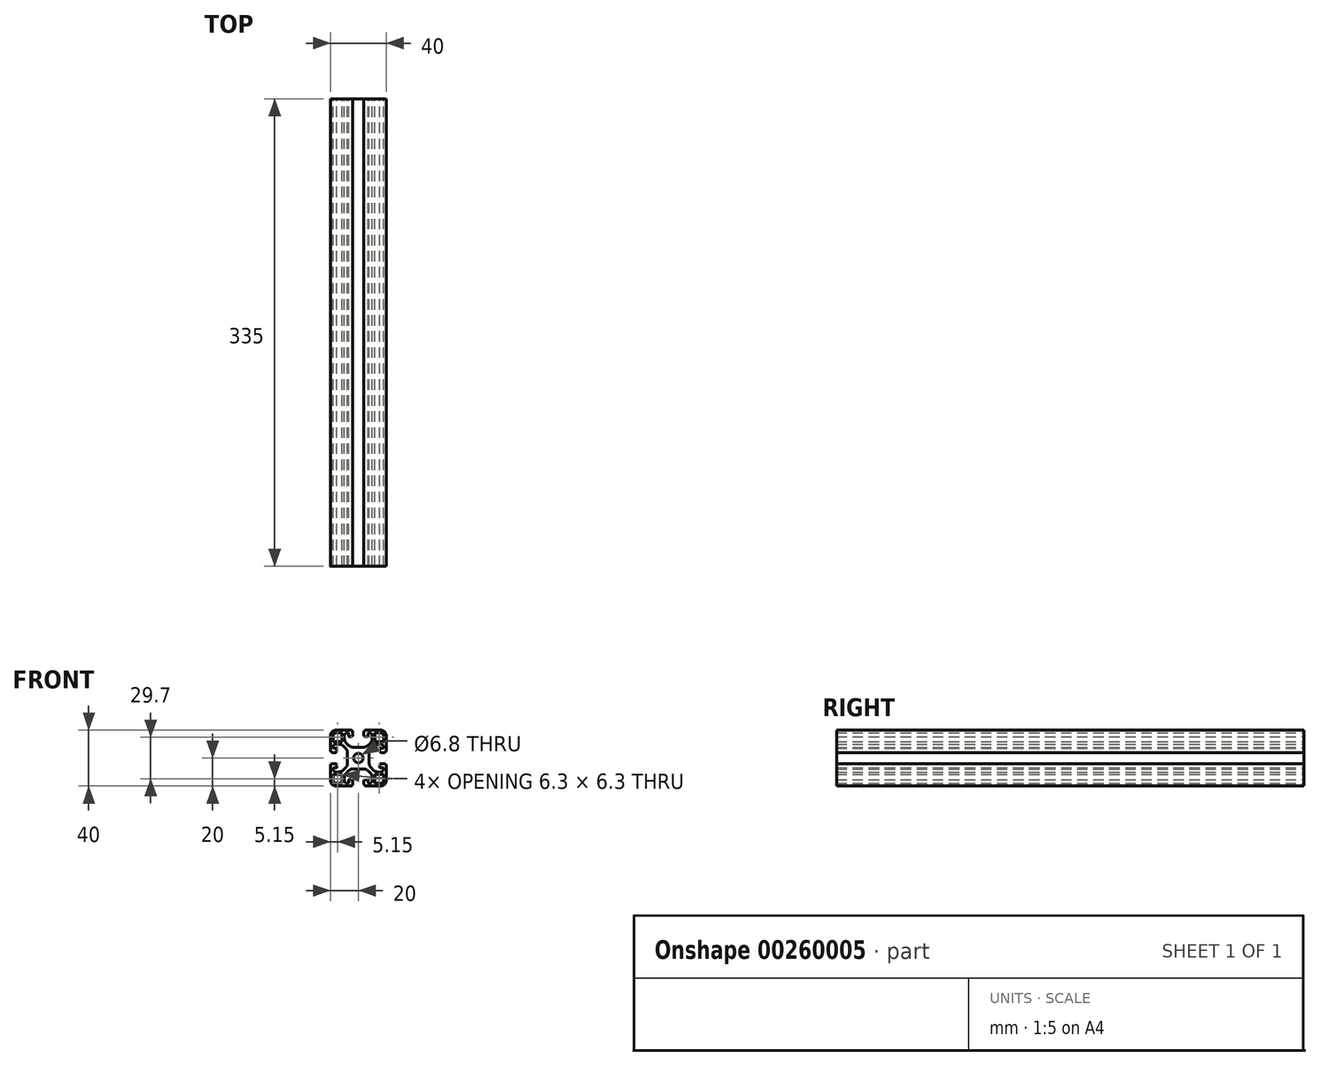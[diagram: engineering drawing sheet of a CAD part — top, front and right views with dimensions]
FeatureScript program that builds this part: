
annotation { "Feature Type Name" : "Feature", "Feature Type Description" : "" }
export const myFeature = defineFeature(function(context is Context, id is Id, definition is map)
    precondition{}
    {
        {
            var Q0;
            Q0=qCreatedBy(makeId("Front.planeOp"),FACE);
            var sketch = newSketch(context, id + "F0", { "sketchPlane" : qUnion([Q0])});
            skCircle(sketch, "E0", {"center": v(0, 0) * mm, "radius": 3.4 * mm});
            skLineSegment(sketch, "E1", {"start": v(0, 0) * mm, "end": v(20, 0) * mm, "construction": true});
            skLineSegment(sketch, "E2", {"start": v(0, 0) * mm, "end": v(20, 20) * mm, "construction": true});
            skLineSegment(sketch, "E3", {"start": v(7.75, 0) * mm, "end": v(7.75, 3.56) * mm});
            skLineSegment(sketch, "E4", {"start": v(9.21, 7.1) * mm, "end": v(10.66, 8.54) * mm});
            skLineSegment(sketch, "E5", {"start": v(20, 5.5) * mm, "end": v(20, 16) * mm});
            skLineSegment(sketch, "E6", {"start": v(18.5, 4) * mm, "end": v(16.35, 4) * mm});
            skLineSegment(sketch, "E7", {"start": v(15.35, 5) * mm, "end": v(15.35, 6.5) * mm});
            skLineSegment(sketch, "E8", {"start": v(15.85, 7) * mm, "end": v(17.5, 7) * mm});
            skLineSegment(sketch, "E9", {"start": v(18, 7.5) * mm, "end": v(18, 8) * mm});
            skLineSegment(sketch, "E10", {"start": v(16, 10) * mm, "end": v(14.2, 10) * mm});
            skPoint(sketch, "E11.visualSharp", {"position": v(7.75, 5.63) * mm});
            skArc(sketch, "E11.filletArc", {"start": v(9.21, 7.1) * mm, "mid": v(8.13, 5.47) * mm, "end": v(7.75, 3.56) * mm});
            skPoint(sketch, "E12.visualSharp", {"position": v(12.12, 10) * mm});
            skArc(sketch, "E12.filletArc", {"start": v(14.2, 10) * mm, "mid": v(12.28, 9.62) * mm, "end": v(10.66, 8.54) * mm});
            skPoint(sketch, "E13.visualSharp", {"position": v(18, 10) * mm});
            skArc(sketch, "E13.filletArc", {"start": v(18, 8) * mm, "mid": v(17.41, 9.41) * mm, "end": v(16, 10) * mm});
            skPoint(sketch, "E14.visualSharp", {"position": v(18, 7) * mm});
            skArc(sketch, "E14.filletArc", {"start": v(17.5, 7) * mm, "mid": v(17.85, 7.15) * mm, "end": v(18, 7.5) * mm});
            skPoint(sketch, "E15.visualSharp", {"position": v(15.35, 7) * mm});
            skArc(sketch, "E15.filletArc", {"start": v(15.85, 7) * mm, "mid": v(15.5, 6.85) * mm, "end": v(15.35, 6.5) * mm});
            skPoint(sketch, "E16.visualSharp", {"position": v(15.35, 4) * mm});
            skArc(sketch, "E16.filletArc", {"start": v(15.35, 5) * mm, "mid": v(15.64, 4.3) * mm, "end": v(16.35, 4) * mm});
            skPoint(sketch, "E17.visualSharp", {"position": v(20, 4) * mm});
            skArc(sketch, "E17.filletArc", {"start": v(18.5, 4) * mm, "mid": v(19.56, 4.44) * mm, "end": v(20, 5.5) * mm});
            skLineSegment(sketch, "E18.MirrorCS", {"start": v(5.5, 20) * mm, "end": v(16, 20) * mm});
            skArc(sketch, "E19.MirrorCS", {"start": v(4, 18.5) * mm, "mid": v(4.44, 19.56) * mm, "end": v(5.5, 20) * mm});
            skLineSegment(sketch, "E20.MirrorCS", {"start": v(4, 18.5) * mm, "end": v(4, 16.35) * mm});
            skArc(sketch, "E21.MirrorCS", {"start": v(5, 15.35) * mm, "mid": v(4.3, 15.64) * mm, "end": v(4, 16.35) * mm});
            skLineSegment(sketch, "E22.MirrorCS", {"start": v(5, 15.35) * mm, "end": v(6.5, 15.35) * mm});
            skArc(sketch, "E23.MirrorCS", {"start": v(7, 15.85) * mm, "mid": v(6.85, 15.5) * mm, "end": v(6.5, 15.35) * mm});
            skLineSegment(sketch, "E24.MirrorCS", {"start": v(7, 15.85) * mm, "end": v(7, 17.5) * mm});
            skArc(sketch, "E25.MirrorCS", {"start": v(7, 17.5) * mm, "mid": v(7.15, 17.85) * mm, "end": v(7.5, 18) * mm});
            skLineSegment(sketch, "E26.MirrorCS", {"start": v(7.5, 18) * mm, "end": v(8, 18) * mm});
            skArc(sketch, "E27.MirrorCS", {"start": v(8, 18) * mm, "mid": v(9.41, 17.41) * mm, "end": v(10, 16) * mm});
            skLineSegment(sketch, "E28.MirrorCS", {"start": v(10, 16) * mm, "end": v(10, 14.2) * mm});
            skArc(sketch, "E29.MirrorCS", {"start": v(10, 14.2) * mm, "mid": v(9.62, 12.28) * mm, "end": v(8.54, 10.66) * mm});
            skLineSegment(sketch, "E30.MirrorCS", {"start": v(7.1, 9.21) * mm, "end": v(8.54, 10.66) * mm});
            skArc(sketch, "E31.MirrorCS", {"start": v(7.1, 9.21) * mm, "mid": v(5.47, 8.13) * mm, "end": v(3.56, 7.75) * mm});
            skLineSegment(sketch, "E32.MirrorCS", {"start": v(0, 7.75) * mm, "end": v(3.56, 7.75) * mm});
            skPoint(sketch, "E33.visualSharp", {"position": v(20, 20) * mm});
            skArc(sketch, "E33.filletArc", {"start": v(20, 16) * mm, "mid": v(18.83, 18.83) * mm, "end": v(16, 20) * mm});
            skLineSegment(sketch, "E34", {"start": v(12.2, 11.7) * mm, "end": v(17.5, 11.7) * mm});
            skLineSegment(sketch, "E35", {"start": v(18, 12.2) * mm, "end": v(18, 16) * mm});
            skLineSegment(sketch, "E36.MirrorCS", {"start": v(11.7, 12.2) * mm, "end": v(11.7, 17.5) * mm});
            skLineSegment(sketch, "E37.MirrorCS", {"start": v(12.2, 18) * mm, "end": v(16, 18) * mm});
            skPoint(sketch, "E38.visualSharp", {"position": v(18, 18) * mm});
            skArc(sketch, "E38.filletArc", {"start": v(18, 16) * mm, "mid": v(17.41, 17.41) * mm, "end": v(16, 18) * mm});
            skPoint(sketch, "E39.visualSharp", {"position": v(18, 11.7) * mm});
            skArc(sketch, "E39.filletArc", {"start": v(17.5, 11.7) * mm, "mid": v(17.85, 11.85) * mm, "end": v(18, 12.2) * mm});
            skPoint(sketch, "E40.visualSharp", {"position": v(11.7, 18) * mm});
            skArc(sketch, "E40.filletArc", {"start": v(12.2, 18) * mm, "mid": v(11.85, 17.85) * mm, "end": v(11.7, 17.5) * mm});
            skPoint(sketch, "E41.visualSharp", {"position": v(11.7, 11.7) * mm});
            skArc(sketch, "E41.filletArc", {"start": v(11.7, 12.2) * mm, "mid": v(11.85, 11.85) * mm, "end": v(12.2, 11.7) * mm});
            skLineSegment(sketch, "E42.MirrorCS", {"start": v(7.75, 0) * mm, "end": v(7.75, -3.56) * mm});
            skArc(sketch, "E43.MirrorCS", {"start": v(9.21, -7.1) * mm, "mid": v(8.13, -5.47) * mm, "end": v(7.75, -3.56) * mm});
            skLineSegment(sketch, "E44.MirrorCS", {"start": v(9.21, -7.1) * mm, "end": v(10.66, -8.54) * mm});
            skArc(sketch, "E45.MirrorCS", {"start": v(14.2, -10) * mm, "mid": v(12.28, -9.62) * mm, "end": v(10.66, -8.54) * mm});
            skLineSegment(sketch, "E46.MirrorCS", {"start": v(16, -10) * mm, "end": v(14.2, -10) * mm});
            skArc(sketch, "E47.MirrorCS", {"start": v(18, -8) * mm, "mid": v(17.41, -9.41) * mm, "end": v(16, -10) * mm});
            skLineSegment(sketch, "E48.MirrorCS", {"start": v(18, -7.5) * mm, "end": v(18, -8) * mm});
            skArc(sketch, "E49.MirrorCS", {"start": v(17.5, -7) * mm, "mid": v(17.85, -7.15) * mm, "end": v(18, -7.5) * mm});
            skLineSegment(sketch, "E50.MirrorCS", {"start": v(15.85, -7) * mm, "end": v(17.5, -7) * mm});
            skArc(sketch, "E51.MirrorCS", {"start": v(15.85, -7) * mm, "mid": v(15.5, -6.85) * mm, "end": v(15.35, -6.5) * mm});
            skLineSegment(sketch, "E52.MirrorCS", {"start": v(15.35, -5) * mm, "end": v(15.35, -6.5) * mm});
            skArc(sketch, "E53.MirrorCS", {"start": v(15.35, -5) * mm, "mid": v(15.64, -4.3) * mm, "end": v(16.35, -4) * mm});
            skLineSegment(sketch, "E54.MirrorCS", {"start": v(18.5, -4) * mm, "end": v(16.35, -4) * mm});
            skArc(sketch, "E55.MirrorCS", {"start": v(18.5, -4) * mm, "mid": v(19.56, -4.44) * mm, "end": v(20, -5.5) * mm});
            skLineSegment(sketch, "E56.MirrorCS", {"start": v(20, -5.5) * mm, "end": v(20, -16) * mm});
            skArc(sketch, "E57.MirrorCS", {"start": v(20, -16) * mm, "mid": v(18.83, -18.83) * mm, "end": v(16, -20) * mm});
            skLineSegment(sketch, "E58.MirrorCS", {"start": v(5.5, -20) * mm, "end": v(16, -20) * mm});
            skArc(sketch, "E59.MirrorCS", {"start": v(4, -18.5) * mm, "mid": v(4.44, -19.56) * mm, "end": v(5.5, -20) * mm});
            skLineSegment(sketch, "E60.MirrorCS", {"start": v(4, -18.5) * mm, "end": v(4, -16.35) * mm});
            skArc(sketch, "E61.MirrorCS", {"start": v(5, -15.35) * mm, "mid": v(4.3, -15.64) * mm, "end": v(4, -16.35) * mm});
            skLineSegment(sketch, "E62.MirrorCS", {"start": v(5, -15.35) * mm, "end": v(6.5, -15.35) * mm});
            skArc(sketch, "E63.MirrorCS", {"start": v(7, -15.85) * mm, "mid": v(6.85, -15.5) * mm, "end": v(6.5, -15.35) * mm});
            skLineSegment(sketch, "E64.MirrorCS", {"start": v(7, -15.85) * mm, "end": v(7, -17.5) * mm});
            skArc(sketch, "E65.MirrorCS", {"start": v(7, -17.5) * mm, "mid": v(7.15, -17.85) * mm, "end": v(7.5, -18) * mm});
            skLineSegment(sketch, "E66.MirrorCS", {"start": v(7.5, -18) * mm, "end": v(8, -18) * mm});
            skArc(sketch, "E67.MirrorCS", {"start": v(8, -18) * mm, "mid": v(9.41, -17.41) * mm, "end": v(10, -16) * mm});
            skLineSegment(sketch, "E68.MirrorCS", {"start": v(10, -16) * mm, "end": v(10, -14.2) * mm});
            skArc(sketch, "E69.MirrorCS", {"start": v(10, -14.2) * mm, "mid": v(9.62, -12.28) * mm, "end": v(8.54, -10.66) * mm});
            skLineSegment(sketch, "E70.MirrorCS", {"start": v(7.1, -9.21) * mm, "end": v(8.54, -10.66) * mm});
            skArc(sketch, "E71.MirrorCS", {"start": v(7.1, -9.21) * mm, "mid": v(5.47, -8.13) * mm, "end": v(3.56, -7.75) * mm});
            skLineSegment(sketch, "E72.MirrorCS", {"start": v(0, -7.75) * mm, "end": v(3.56, -7.75) * mm});
            skLineSegment(sketch, "E73.MirrorCS", {"start": v(12.2, -11.7) * mm, "end": v(17.5, -11.7) * mm});
            skArc(sketch, "E74.MirrorCS", {"start": v(17.5, -11.7) * mm, "mid": v(17.85, -11.85) * mm, "end": v(18, -12.2) * mm});
            skLineSegment(sketch, "E75.MirrorCS", {"start": v(18, -12.2) * mm, "end": v(18, -16) * mm});
            skArc(sketch, "E76.MirrorCS", {"start": v(18, -16) * mm, "mid": v(17.41, -17.41) * mm, "end": v(16, -18) * mm});
            skLineSegment(sketch, "E77.MirrorCS", {"start": v(12.2, -18) * mm, "end": v(16, -18) * mm});
            skArc(sketch, "E78.MirrorCS", {"start": v(12.2, -18) * mm, "mid": v(11.85, -17.85) * mm, "end": v(11.7, -17.5) * mm});
            skLineSegment(sketch, "E79.MirrorCS", {"start": v(11.7, -12.2) * mm, "end": v(11.7, -17.5) * mm});
            skArc(sketch, "E80.MirrorCS", {"start": v(11.7, -12.2) * mm, "mid": v(11.85, -11.85) * mm, "end": v(12.2, -11.7) * mm});
            skLineSegment(sketch, "E81", {"start": v(0, 0) * mm, "end": v(0, 20) * mm, "construction": true});
            skLineSegment(sketch, "E82.MirrorCS", {"start": v(0, 7.75) * mm, "end": v(-3.56, 7.75) * mm});
            skArc(sketch, "E83.MirrorCS", {"start": v(-7.1, 9.21) * mm, "mid": v(-5.47, 8.13) * mm, "end": v(-3.56, 7.75) * mm});
            skLineSegment(sketch, "E84.MirrorCS", {"start": v(-7.1, 9.21) * mm, "end": v(-8.54, 10.66) * mm});
            skArc(sketch, "E85.MirrorCS", {"start": v(-10, 14.2) * mm, "mid": v(-9.62, 12.28) * mm, "end": v(-8.54, 10.66) * mm});
            skLineSegment(sketch, "E86.MirrorCS", {"start": v(-10, 16) * mm, "end": v(-10, 14.2) * mm});
            skArc(sketch, "E87.MirrorCS", {"start": v(-8, 18) * mm, "mid": v(-9.41, 17.41) * mm, "end": v(-10, 16) * mm});
            skLineSegment(sketch, "E88.MirrorCS", {"start": v(-7.5, 18) * mm, "end": v(-8, 18) * mm});
            skArc(sketch, "E89.MirrorCS", {"start": v(-7, 17.5) * mm, "mid": v(-7.15, 17.85) * mm, "end": v(-7.5, 18) * mm});
            skLineSegment(sketch, "E90.MirrorCS", {"start": v(-7, 15.85) * mm, "end": v(-7, 17.5) * mm});
            skArc(sketch, "E91.MirrorCS", {"start": v(-7, 15.85) * mm, "mid": v(-6.85, 15.5) * mm, "end": v(-6.5, 15.35) * mm});
            skLineSegment(sketch, "E92.MirrorCS", {"start": v(-5, 15.35) * mm, "end": v(-6.5, 15.35) * mm});
            skArc(sketch, "E93.MirrorCS", {"start": v(-5, 15.35) * mm, "mid": v(-4.3, 15.64) * mm, "end": v(-4, 16.35) * mm});
            skLineSegment(sketch, "E94.MirrorCS", {"start": v(-4, 18.5) * mm, "end": v(-4, 16.35) * mm});
            skArc(sketch, "E95.MirrorCS", {"start": v(-4, 18.5) * mm, "mid": v(-4.44, 19.56) * mm, "end": v(-5.5, 20) * mm});
            skLineSegment(sketch, "E96.MirrorCS", {"start": v(-5.5, 20) * mm, "end": v(-16, 20) * mm});
            skArc(sketch, "E97.MirrorCS", {"start": v(-20, 16) * mm, "mid": v(-18.83, 18.83) * mm, "end": v(-16, 20) * mm});
            skLineSegment(sketch, "E98.MirrorCS", {"start": v(-20, 5.5) * mm, "end": v(-20, 16) * mm});
            skArc(sketch, "E99.MirrorCS", {"start": v(-18.5, 4) * mm, "mid": v(-19.56, 4.44) * mm, "end": v(-20, 5.5) * mm});
            skLineSegment(sketch, "E100.MirrorCS", {"start": v(-18.5, 4) * mm, "end": v(-16.35, 4) * mm});
            skArc(sketch, "E101.MirrorCS", {"start": v(-15.35, 5) * mm, "mid": v(-15.64, 4.3) * mm, "end": v(-16.35, 4) * mm});
            skLineSegment(sketch, "E102.MirrorCS", {"start": v(-15.35, 5) * mm, "end": v(-15.35, 6.5) * mm});
            skArc(sketch, "E103.MirrorCS", {"start": v(-15.85, 7) * mm, "mid": v(-15.5, 6.85) * mm, "end": v(-15.35, 6.5) * mm});
            skLineSegment(sketch, "E104.MirrorCS", {"start": v(-15.85, 7) * mm, "end": v(-17.5, 7) * mm});
            skArc(sketch, "E105.MirrorCS", {"start": v(-17.5, 7) * mm, "mid": v(-17.85, 7.15) * mm, "end": v(-18, 7.5) * mm});
            skLineSegment(sketch, "E106.MirrorCS", {"start": v(-18, 7.5) * mm, "end": v(-18, 8) * mm});
            skArc(sketch, "E107.MirrorCS", {"start": v(-18, 8) * mm, "mid": v(-17.41, 9.41) * mm, "end": v(-16, 10) * mm});
            skLineSegment(sketch, "E108.MirrorCS", {"start": v(-16, 10) * mm, "end": v(-14.2, 10) * mm});
            skArc(sketch, "E109.MirrorCS", {"start": v(-14.2, 10) * mm, "mid": v(-12.28, 9.62) * mm, "end": v(-10.66, 8.54) * mm});
            skLineSegment(sketch, "E110.MirrorCS", {"start": v(-9.21, 7.1) * mm, "end": v(-10.66, 8.54) * mm});
            skArc(sketch, "E111.MirrorCS", {"start": v(-9.21, 7.1) * mm, "mid": v(-8.13, 5.47) * mm, "end": v(-7.75, 3.56) * mm});
            skLineSegment(sketch, "E112.MirrorCS", {"start": v(-7.75, 0) * mm, "end": v(-7.75, 3.56) * mm});
            skLineSegment(sketch, "E113.MirrorCS", {"start": v(-7.75, 0) * mm, "end": v(-7.75, -3.56) * mm});
            skArc(sketch, "E114.MirrorCS", {"start": v(-9.21, -7.1) * mm, "mid": v(-8.13, -5.47) * mm, "end": v(-7.75, -3.56) * mm});
            skLineSegment(sketch, "E115.MirrorCS", {"start": v(-9.21, -7.1) * mm, "end": v(-10.66, -8.54) * mm});
            skArc(sketch, "E116.MirrorCS", {"start": v(-14.2, -10) * mm, "mid": v(-12.28, -9.62) * mm, "end": v(-10.66, -8.54) * mm});
            skLineSegment(sketch, "E117.MirrorCS", {"start": v(-16, -10) * mm, "end": v(-14.2, -10) * mm});
            skArc(sketch, "E118.MirrorCS", {"start": v(-18, -8) * mm, "mid": v(-17.41, -9.41) * mm, "end": v(-16, -10) * mm});
            skLineSegment(sketch, "E119.MirrorCS", {"start": v(-18, -7.5) * mm, "end": v(-18, -8) * mm});
            skArc(sketch, "E120.MirrorCS", {"start": v(-17.5, -7) * mm, "mid": v(-17.85, -7.15) * mm, "end": v(-18, -7.5) * mm});
            skLineSegment(sketch, "E121.MirrorCS", {"start": v(-15.85, -7) * mm, "end": v(-17.5, -7) * mm});
            skArc(sketch, "E122.MirrorCS", {"start": v(-15.85, -7) * mm, "mid": v(-15.5, -6.85) * mm, "end": v(-15.35, -6.5) * mm});
            skLineSegment(sketch, "E123.MirrorCS", {"start": v(-15.35, -5) * mm, "end": v(-15.35, -6.5) * mm});
            skArc(sketch, "E124.MirrorCS", {"start": v(-15.35, -5) * mm, "mid": v(-15.64, -4.3) * mm, "end": v(-16.35, -4) * mm});
            skLineSegment(sketch, "E125.MirrorCS", {"start": v(-18.5, -4) * mm, "end": v(-16.35, -4) * mm});
            skArc(sketch, "E126.MirrorCS", {"start": v(-18.5, -4) * mm, "mid": v(-19.56, -4.44) * mm, "end": v(-20, -5.5) * mm});
            skLineSegment(sketch, "E127.MirrorCS", {"start": v(-20, -5.5) * mm, "end": v(-20, -16) * mm});
            skArc(sketch, "E128.MirrorCS", {"start": v(-20, -16) * mm, "mid": v(-18.83, -18.83) * mm, "end": v(-16, -20) * mm});
            skLineSegment(sketch, "E129.MirrorCS", {"start": v(-5.5, -20) * mm, "end": v(-16, -20) * mm});
            skArc(sketch, "E130.MirrorCS", {"start": v(-4, -18.5) * mm, "mid": v(-4.44, -19.56) * mm, "end": v(-5.5, -20) * mm});
            skLineSegment(sketch, "E131.MirrorCS", {"start": v(-4, -18.5) * mm, "end": v(-4, -16.35) * mm});
            skArc(sketch, "E132.MirrorCS", {"start": v(-5, -15.35) * mm, "mid": v(-4.3, -15.64) * mm, "end": v(-4, -16.35) * mm});
            skLineSegment(sketch, "E133.MirrorCS", {"start": v(-5, -15.35) * mm, "end": v(-6.5, -15.35) * mm});
            skArc(sketch, "E134.MirrorCS", {"start": v(-7, -15.85) * mm, "mid": v(-6.85, -15.5) * mm, "end": v(-6.5, -15.35) * mm});
            skLineSegment(sketch, "E135.MirrorCS", {"start": v(-7, -15.85) * mm, "end": v(-7, -17.5) * mm});
            skArc(sketch, "E136.MirrorCS", {"start": v(-7, -17.5) * mm, "mid": v(-7.15, -17.85) * mm, "end": v(-7.5, -18) * mm});
            skLineSegment(sketch, "E137.MirrorCS", {"start": v(-7.5, -18) * mm, "end": v(-8, -18) * mm});
            skArc(sketch, "E138.MirrorCS", {"start": v(-8, -18) * mm, "mid": v(-9.41, -17.41) * mm, "end": v(-10, -16) * mm});
            skLineSegment(sketch, "E139.MirrorCS", {"start": v(-10, -16) * mm, "end": v(-10, -14.2) * mm});
            skArc(sketch, "E140.MirrorCS", {"start": v(-10, -14.2) * mm, "mid": v(-9.62, -12.28) * mm, "end": v(-8.54, -10.66) * mm});
            skLineSegment(sketch, "E141.MirrorCS", {"start": v(-7.1, -9.21) * mm, "end": v(-8.54, -10.66) * mm});
            skArc(sketch, "E142.MirrorCS", {"start": v(-7.1, -9.21) * mm, "mid": v(-5.47, -8.13) * mm, "end": v(-3.56, -7.75) * mm});
            skLineSegment(sketch, "E143.MirrorCS", {"start": v(0, -7.75) * mm, "end": v(-3.56, -7.75) * mm});
            skLineSegment(sketch, "E144.MirrorCS", {"start": v(-12.2, 11.7) * mm, "end": v(-17.5, 11.7) * mm});
            skArc(sketch, "E145.MirrorCS", {"start": v(-17.5, 11.7) * mm, "mid": v(-17.85, 11.85) * mm, "end": v(-18, 12.2) * mm});
            skLineSegment(sketch, "E146.MirrorCS", {"start": v(-18, 12.2) * mm, "end": v(-18, 16) * mm});
            skArc(sketch, "E147.MirrorCS", {"start": v(-18, 16) * mm, "mid": v(-17.41, 17.41) * mm, "end": v(-16, 18) * mm});
            skLineSegment(sketch, "E148.MirrorCS", {"start": v(-12.2, 18) * mm, "end": v(-16, 18) * mm});
            skArc(sketch, "E149.MirrorCS", {"start": v(-12.2, 18) * mm, "mid": v(-11.85, 17.85) * mm, "end": v(-11.7, 17.5) * mm});
            skLineSegment(sketch, "E150.MirrorCS", {"start": v(-11.7, 12.2) * mm, "end": v(-11.7, 17.5) * mm});
            skArc(sketch, "E151.MirrorCS", {"start": v(-11.7, 12.2) * mm, "mid": v(-11.85, 11.85) * mm, "end": v(-12.2, 11.7) * mm});
            skLineSegment(sketch, "E152.MirrorCS", {"start": v(-12.2, -11.7) * mm, "end": v(-17.5, -11.7) * mm});
            skArc(sketch, "E153.MirrorCS", {"start": v(-17.5, -11.7) * mm, "mid": v(-17.85, -11.85) * mm, "end": v(-18, -12.2) * mm});
            skLineSegment(sketch, "E154.MirrorCS", {"start": v(-18, -12.2) * mm, "end": v(-18, -16) * mm});
            skArc(sketch, "E155.MirrorCS", {"start": v(-18, -16) * mm, "mid": v(-17.41, -17.41) * mm, "end": v(-16, -18) * mm});
            skLineSegment(sketch, "E156.MirrorCS", {"start": v(-12.2, -18) * mm, "end": v(-16, -18) * mm});
            skArc(sketch, "E157.MirrorCS", {"start": v(-12.2, -18) * mm, "mid": v(-11.85, -17.85) * mm, "end": v(-11.7, -17.5) * mm});
            skLineSegment(sketch, "E158.MirrorCS", {"start": v(-11.7, -12.2) * mm, "end": v(-11.7, -17.5) * mm});
            skArc(sketch, "E159.MirrorCS", {"start": v(-11.7, -12.2) * mm, "mid": v(-11.85, -11.85) * mm, "end": v(-12.2, -11.7) * mm});
            skSolve(sketch);
        }
        {
            var Q0;
            Q0=makeQuery(id+"F0.imprint","IMPRINT",FACE,{"disambiguationData":[TD([[makeQuery(id+"F0.imprint","IMPRINT",EDGE,{"derivedFrom":sQuery(id+"F0.wireOp",EDGE,"E0")}),-1.0]])]});
            extrude(context, id + "F1", {"entities" : qUnion([Q0]), "depth" : 335 * mm, "offsetDistance" : 25 * mm});
        }
    });
